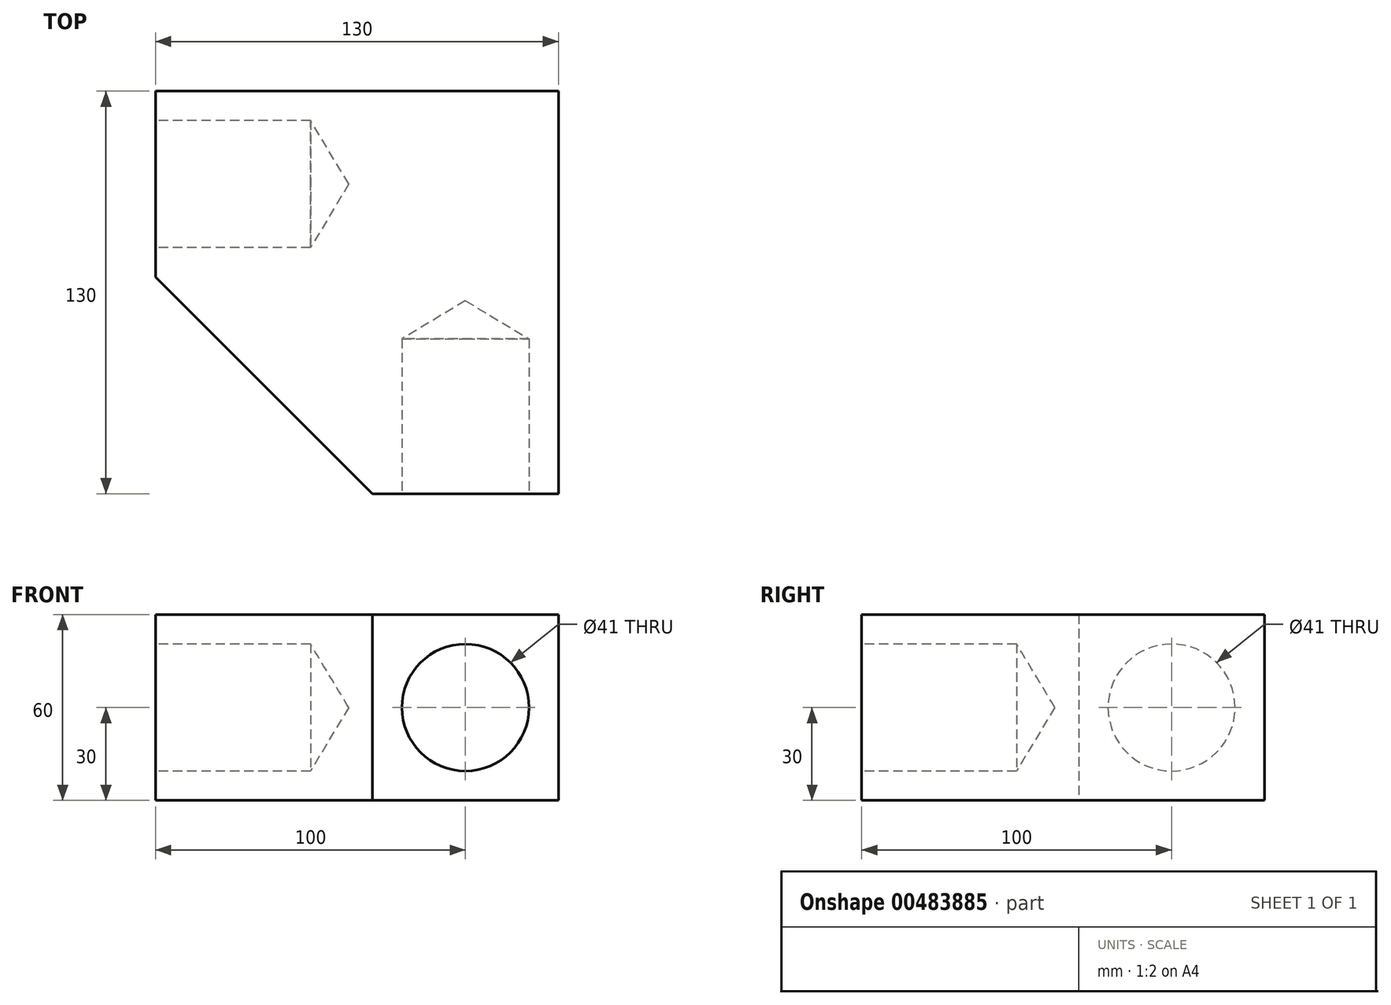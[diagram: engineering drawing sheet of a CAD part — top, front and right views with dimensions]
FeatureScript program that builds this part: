
annotation { "Feature Type Name" : "Feature", "Feature Type Description" : "" }
export const myFeature = defineFeature(function(context is Context, id is Id, definition is map)
    precondition{}
    {
        {
            var Q0;
            Q0=qCreatedBy(makeId("Top.planeOp"),FACE);
            var sketch = newSketch(context, id + "F0", { "sketchPlane" : qUnion([Q0])});
            skLineSegment(sketch, "E0.bottom", {"start": v(0, 60) * mm, "end": v(130, 60) * mm});
            skLineSegment(sketch, "E0.top", {"start": v(0, 0) * mm, "end": v(70, 0) * mm});
            skLineSegment(sketch, "E0.left", {"start": v(0, 60) * mm, "end": v(0, 0) * mm});
            skLineSegment(sketch, "E1", {"start": v(130, 0) * mm, "end": v(130, 0) * mm});
            skLineSegment(sketch, "E2", {"start": v(70, 0) * mm, "end": v(130, 60) * mm});
            skLineSegment(sketch, "E3", {"start": v(0, 60) * mm, "end": v(0, 60) * mm});
            skLineSegment(sketch, "E4", {"start": v(0, 60) * mm, "end": v(0, 30) * mm});
            skLineSegment(sketch, "E5", {"start": v(0, 30) * mm, "end": v(40, 30) * mm});
            skSolve(sketch);
        }
        {
            var Q0;
            Q0 = qSketchRegion(id + "F0", true);
            extrude(context, id + "F1", {"entities" : qUnion([Q0]), "depth" : 60 * mm});
        }
        {
            var Q0;
            Q0=makeQuery(id+"F1.opExtrude","SWEPT_FACE",FACE,{"disambiguationData":[OSD([sQuery(id+"F0.wireOp",EDGE,"E0.left"),sQuery(id+"F0.wireOp",EDGE,"E4")])]});
            var sketch = newSketch(context, id + "F2", { "sketchPlane" : qUnion([Q0])});
            skLineSegment(sketch, "E6", {"start": v(-30, 0) * mm, "end": v(-30, 30) * mm});
            skSolve(sketch);
        }
        {
            var Q0;
            Q0=sQuery(id+"F2.wireOp",VERTEX,"E6.end");
            var Q1;
            Q1=makeQuery(id+"F1.opExtrude","SWEPT_BODY",BODY,{"disambiguationData":[OSD([sQuery(id+"F0.wireOp",EDGE,"E0.bottom"),sQuery(id+"F0.wireOp",EDGE,"E0.top"),sQuery(id+"F0.wireOp",EDGE,"E0.left"),sQuery(id+"F0.wireOp",EDGE,"E2"),sQuery(id+"F0.wireOp",EDGE,"E4")])]});
            hole(context, id + "F3", {"style" : HoleStyle.SIMPLE, "endStyle" : HoleEndStyle.BLIND, "holeDiameter" : 41 * mm, "holeDepth" : 50 * mm, "isTappedThrough" : true, "tappedDepth" : 12 * mm, "tapClearance" : 3, "locations" : qUnion([Q0]), "scope" : qUnion([Q1])});
        }
        {
            var Q0;
            Q0=makeQuery(id+"F1.opExtrude","SWEPT_BODY",BODY,{"disambiguationData":[OSD([sQuery(id+"F0.wireOp",EDGE,"E0.bottom"),sQuery(id+"F0.wireOp",EDGE,"E0.top"),sQuery(id+"F0.wireOp",EDGE,"E0.left"),sQuery(id+"F0.wireOp",EDGE,"E2"),sQuery(id+"F0.wireOp",EDGE,"E4")])]});
            var Q1;
            Q1=makeQuery(id+"F1.opExtrude","SWEPT_FACE",FACE,{"disambiguationData":[OSD([sQuery(id+"F0.wireOp",EDGE,"E2")])]});
            var Q2;
            Q2=makeQuery(id+"F1.opExtrude","SWEPT_FACE",FACE,{"disambiguationData":[OSD([sQuery(id+"F0.wireOp",EDGE,"E2")])]});
            mirror(context, id + "F4", {"operationType" : NewBodyOperationType.ADD, "entities" : qUnion([Q0]), "faces" : qUnion([Q1]), "mirrorPlane" : qUnion([Q2])});
        }
        {
            var Q0;
            Q0=qCreatedBy(makeId("Top.planeOp"),FACE);
            var sketch = newSketch(context, id + "F5", { "sketchPlane" : qUnion([Q0])});
            skLineSegment(sketch, "E7", {"start": v(0, 0) * mm, "end": v(70, -70) * mm});
            skLineSegment(sketch, "E8", {"start": v(70, -70) * mm, "end": v(70, 0) * mm});
            skLineSegment(sketch, "E9", {"start": v(70, 0) * mm, "end": v(0, 0) * mm});
            skSolve(sketch);
        }
        {
            var Q0;
            Q0 = qSketchRegion(id + "F5", true);
            extrude(context, id + "F6", {"entities" : qUnion([Q0]), "operationType" : NewBodyOperationType.ADD, "depth" : 60 * mm});
        }
    });
